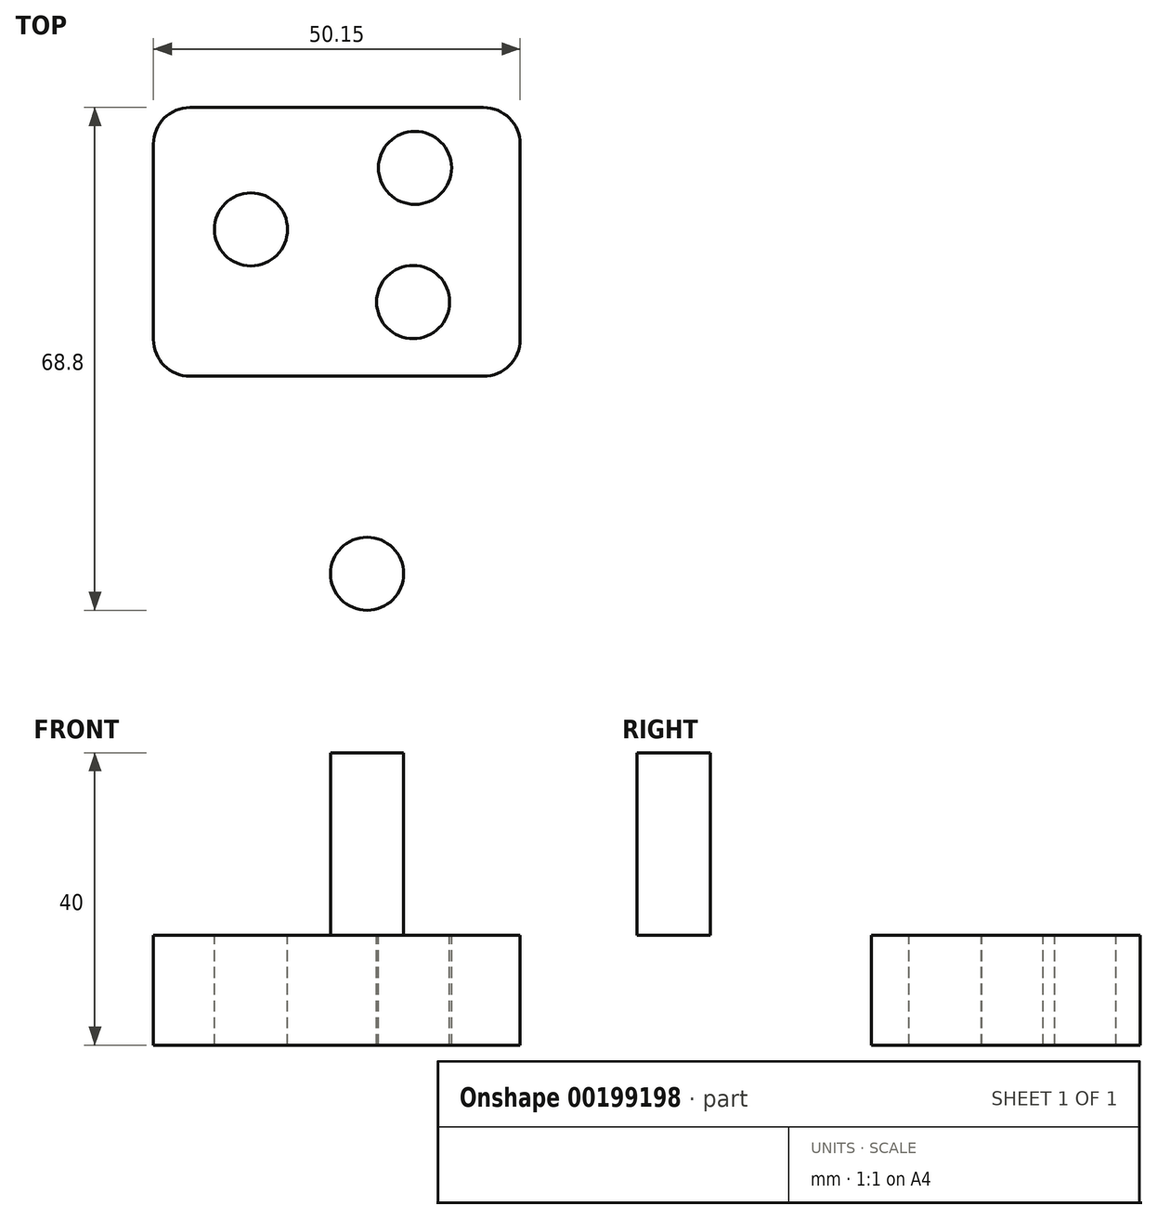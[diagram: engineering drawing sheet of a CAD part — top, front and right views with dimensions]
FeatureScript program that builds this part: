
annotation { "Feature Type Name" : "Feature", "Feature Type Description" : "" }
export const myFeature = defineFeature(function(context is Context, id is Id, definition is map)
    precondition{}
    {
        {
            var Q0;
            Q0=qCreatedBy(makeId("Top.planeOp"),FACE);
            var sketch = newSketch(context, id + "F0", { "sketchPlane" : qUnion([Q0])});
            skLineSegment(sketch, "E0.bottom", {"start": v(0, 0) * mm, "end": v(-50.15, 0) * mm});
            skLineSegment(sketch, "E0.top", {"start": v(0, 36.77) * mm, "end": v(-50.15, 36.77) * mm});
            skLineSegment(sketch, "E0.left", {"start": v(0, 0) * mm, "end": v(0, 36.77) * mm});
            skLineSegment(sketch, "E0.right", {"start": v(-50.15, 0) * mm, "end": v(-50.15, 36.77) * mm});
            skSolve(sketch);
        }
        {
            var Q0;
            Q0 = qSketchRegion(id + "F0", true);
            extrude(context, id + "F1", {"entities" : qUnion([Q0]), "oppositeDirection" : true, "depth" : 15 * mm});
        }
        {
            var Q0;
            Q0=makeQuery(id+"F1.opExtrude","CAP_FACE",FACE,{"disambiguationData":[OSD([sQuery(id+"F0.wireOp",EDGE,"E0.bottom"),sQuery(id+"F0.wireOp",EDGE,"E0.top"),sQuery(id+"F0.wireOp",EDGE,"E0.left"),sQuery(id+"F0.wireOp",EDGE,"E0.right")])],"isStart":true});
            var sketch = newSketch(context, id + "F2", { "sketchPlane" : qUnion([Q0])});
            skCircle(sketch, "E1", {"center": v(-14.38, 28.5) * mm, "radius": 5 * mm});
            skCircle(sketch, "E2", {"center": v(-14.63, 10.14) * mm, "radius": 5 * mm});
            skCircle(sketch, "E3", {"center": v(-36.82, 20.09) * mm, "radius": 5 * mm});
            skSolve(sketch);
        }
        {
            var Q0;
            Q0 = qSketchRegion(id + "F2", true);
            extrude(context, id + "F3", {"entities" : qUnion([Q0]), "operationType" : NewBodyOperationType.REMOVE, "oppositeDirection" : true, "depth" : 25 * mm});
        }
        {
            var Q0;
            Q0=makeQuery(id+"F1.opExtrude","SWEPT_EDGE",EDGE,{"disambiguationData":[OSD([sQuery(id+"F0.wireOp",EDGE,"E0.bottom"),sQuery(id+"F0.wireOp",EDGE,"E0.right")])]});
            var Q1;
            Q1=makeQuery(id+"F1.opExtrude","SWEPT_EDGE",EDGE,{"disambiguationData":[OSD([sQuery(id+"F0.wireOp",EDGE,"E0.bottom"),sQuery(id+"F0.wireOp",EDGE,"E0.left")])]});
            var Q2;
            Q2=makeQuery(id+"F1.opExtrude","SWEPT_EDGE",EDGE,{"disambiguationData":[OSD([sQuery(id+"F0.wireOp",EDGE,"E0.top"),sQuery(id+"F0.wireOp",EDGE,"E0.left")])]});
            var Q3;
            Q3=makeQuery(id+"F1.opExtrude","SWEPT_EDGE",EDGE,{"disambiguationData":[OSD([sQuery(id+"F0.wireOp",EDGE,"E0.top"),sQuery(id+"F0.wireOp",EDGE,"E0.right")])]});
            fillet(context, id + "F4", {"entities" : qUnion([Q0, Q1, Q2, Q3]), "radius" : 5 * mm, "tangentPropagation" : true, "allowEdgeOverflow" : false});
        }
        {
            var Q0;
            Q0=qCreatedBy(makeId("Top.planeOp"),FACE);
            var sketch = newSketch(context, id + "F5", { "sketchPlane" : qUnion([Q0])});
            skCircle(sketch, "E4", {"center": v(-20.94, -27.03) * mm, "radius": 5 * mm});
            skSolve(sketch);
        }
        {
            var Q0;
            Q0 = qSketchRegion(id + "F5", true);
            extrude(context, id + "F6", {"entities" : qUnion([Q0]), "depth" : 25 * mm});
        }
    });
